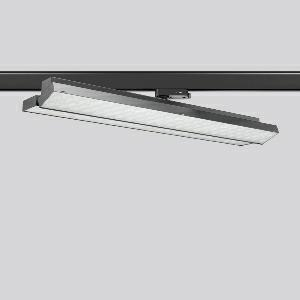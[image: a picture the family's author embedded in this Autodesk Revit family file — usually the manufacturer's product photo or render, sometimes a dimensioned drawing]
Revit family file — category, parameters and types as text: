
# Revit family: tx-move_742161_003_106e
name_source: partatom
category: Lighting Fixtures
units: mm (PartAtom-declared; Revit-internal decimal feet)

## family parameters
Cut with Voids When Loaded = No
Host = Face
Light Source = No
Part Type = Normal
Room Calculation Point = No
Round Connector Dimension = Use Diameter
Shared = No

## types (1)
- MultiLumen 1 (1 x LED Modul 830, 2900 lm, 3000)
    Apparent Load = 41 VA
    CIE Flux Codes = 90 97 99 100 100
    Color Rendering = 80
    Color Temperature = 3000
    Default Elevation = 1800 mm
    Description = Series: TX-MOVE
Multifunctional surface-mounted spotlight for area lighting. Very flat design. Housing: sheet steel, powder-coated. Rotation range: 356°. Swivel range: 90°. Consistent alignment possible with visible tilt scale. High-efficiency LED units with optimum light control thanks to clear plastic (PC) lens optics. Spezielle Mikrostrukturen reduzieren Gelbsaum. Symmetrical light distribution. With multi adaptor for 3-circuit tracks 230 V. Suitable for Track on ceiling. MultiLumen: Luminous flux adjustable in 3 steps. Factory setting is the highest luminous flux. Environmentally friendly and resource-saving due to replaceable and recyclable components. Very good glare control, ideal for till areas. 
Colour: deep black, matt (RAL 9005)
Length: 570 mm
Width: 119 mm
Height: 92 mm
Lamp: LED
Socket: without socket
Colour temperature: 3000K
Colour rendering index (CRI): 80
System power: 41 W
Rated luminous flux: 5800 lm
Luminous efficiency: 141 lm/W
System power 2: 57 W
Rated luminous flux 2: 7850 lm
Luminous efficiency 2: 138 lm/W
System power 3: 73 W
Rated luminous flux 3: 9600 lm
Luminous efficiency 3: 132 lm/W
Control gear: Regulated power supply
Protection class: I
Type of protection: IP 20
    Height = 75 mm
    Lamp = 1 x LED Modul 830
    Lamp Light Flux = 2900 lm
    Lamp count = 1
    Length = 569 mm
    Lifetime = 50000 h
    Luminous efficacy = 141 lm/W
    Manufacturer = RZB
    ModVariant = No
    Model = 742161.003
    Mounting Place = Ceiling
    Mounting Type = Surface mounted
    Number of Poles = 1
    OnlyDefault = Yes
    Power Factor = 1
    Product Name = TX-MOVE
    Product group = Track mounted projectors
    ProductGroupID = 301
    Protection Class = Protection class I
    Protection Degree = IP 20
    RLX_Detail_Level = 1
    RLX_Emergency_Light_Flux = 0 lm
    RLX_Emergency_Type = 0
    RLX_Emergency_Type_DB = No
    RlxData = <blob elided: 36941 chars, md5=84ffdaec>
    Socket = socket
    Standby Power = 0 W
    System Light Flux = 5800 lm
    System Power = 41 W
    Type Comments = MultiLumen 1
    Type Image = 742162.003.jpg
    URL = http://relux.com
    VarID = multilumen_1
    Voltage = 0 V
    Weight = 0.00 kg
    Width = 119 mm

## geometry (parser evidence)
native form markers: Blend x4, Sweep x16
no freeform markers — native parametric forms only
